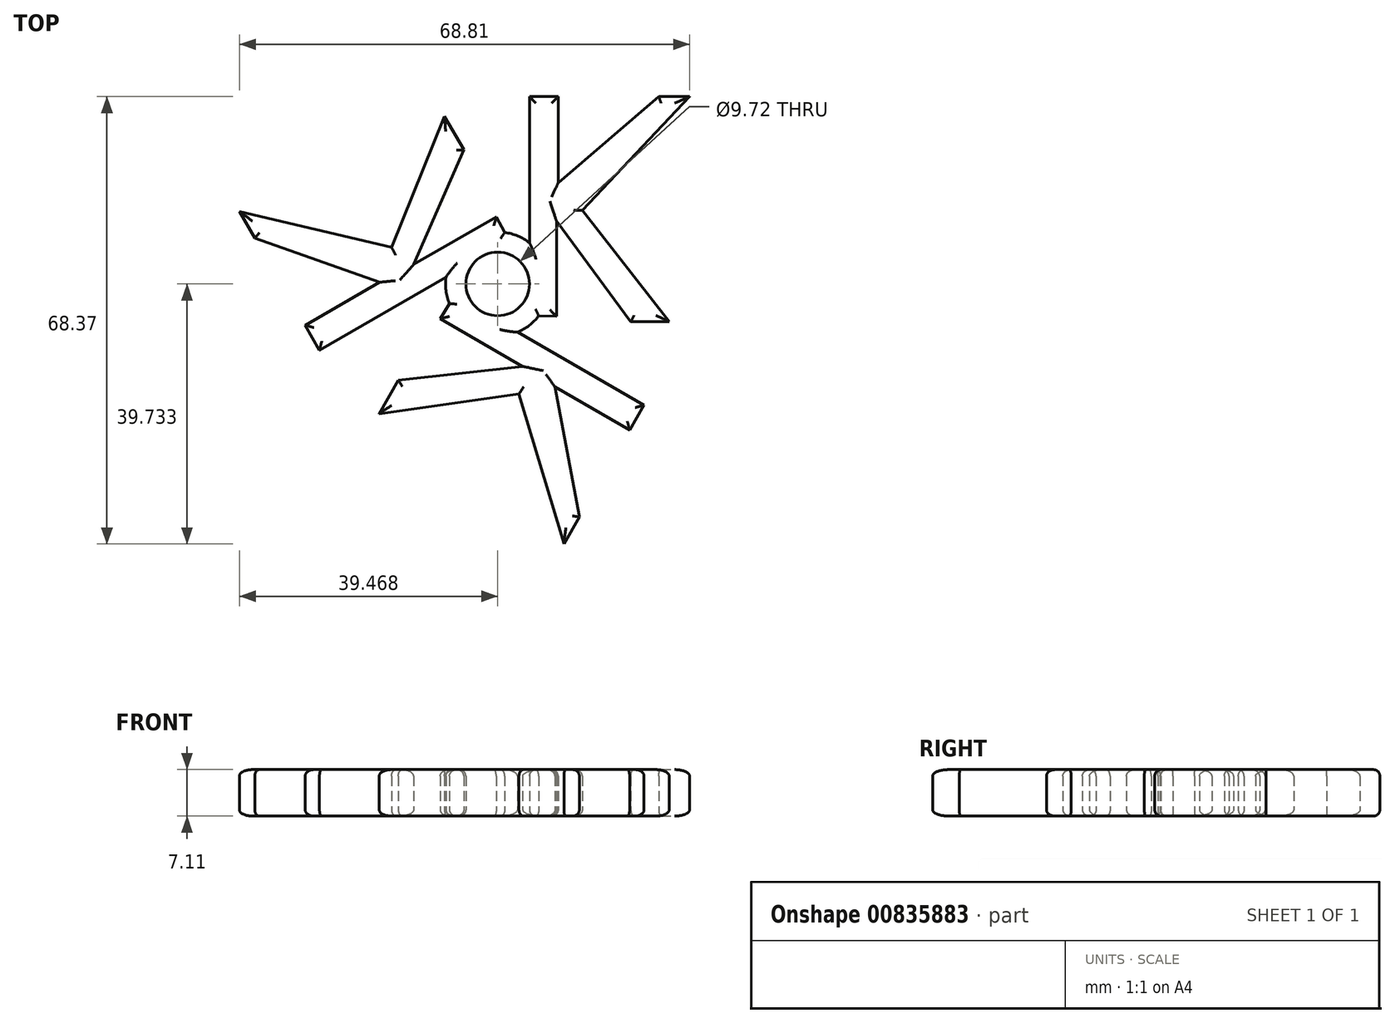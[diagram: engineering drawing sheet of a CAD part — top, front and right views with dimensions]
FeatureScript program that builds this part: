
annotation { "Feature Type Name" : "Feature", "Feature Type Description" : "" }
export const myFeature = defineFeature(function(context is Context, id is Id, definition is map)
    precondition{}
    {
        {
            var Q0;
            Q0=qCreatedBy(makeId("Top.planeOp"),FACE);
            var sketch = newSketch(context, id + "F0", { "sketchPlane" : qUnion([Q0])});
            skText(sketch, "E0", { "text": "K", "fontName": "RobotoSlab-Bold.ttf"});
            skLineSegment(sketch, "E1", {"start": v(-36.74, 28.94) * mm, "end": v(-41.1, 29.85) * mm});
            skLineSegment(sketch, "E2", {"start": v(-41.1, 29.85) * mm, "end": v(-41.1, 34.7) * mm});
            skLineSegment(sketch, "E3", {"start": v(-41.1, 34.7) * mm, "end": v(-24.32, 34.7) * mm});
            skLineSegment(sketch, "E4", {"start": v(-24.32, 34.7) * mm, "end": v(-24.32, 29.8) * mm});
            skLineSegment(sketch, "E5", {"start": v(-24.32, 29.8) * mm, "end": v(-28.43, 28.94) * mm});
            skLineSegment(sketch, "E6", {"start": v(-28.43, 28.94) * mm, "end": v(-28.43, 18) * mm});
            skLineSegment(sketch, "E7", {"start": v(-28.43, 18) * mm, "end": v(-24.89, 18) * mm});
            skLineSegment(sketch, "E8", {"start": v(-24.89, 18) * mm, "end": v(-17.02, 29.37) * mm});
            skLineSegment(sketch, "E9", {"start": v(-17.02, 29.37) * mm, "end": v(-19.35, 29.8) * mm});
            skLineSegment(sketch, "E10", {"start": v(-19.35, 29.8) * mm, "end": v(-19.35, 34.7) * mm});
            skLineSegment(sketch, "E11", {"start": v(-19.35, 34.7) * mm, "end": v(-3, 34.7) * mm});
            skLineSegment(sketch, "E12", {"start": v(-3, 34.7) * mm, "end": v(-3, 29.8) * mm});
            skLineSegment(sketch, "E13", {"start": v(-3, 29.8) * mm, "end": v(-7.33, 29.07) * mm});
            skLineSegment(sketch, "E14", {"start": v(-7.33, 29.07) * mm, "end": v(-17.58, 15.36) * mm});
            skLineSegment(sketch, "E15", {"start": v(-17.58, 15.36) * mm, "end": v(-6.25, -0.86) * mm});
            skLineSegment(sketch, "E16", {"start": v(-6.25, -0.86) * mm, "end": v(-2.14, -1.5) * mm});
            skLineSegment(sketch, "E17", {"start": v(-2.14, -1.5) * mm, "end": v(-2.14, -6.47) * mm});
            skLineSegment(sketch, "E18", {"start": v(-2.14, -6.47) * mm, "end": v(-18.49, -6.47) * mm});
            skLineSegment(sketch, "E19", {"start": v(-18.49, -6.47) * mm, "end": v(-18.49, -1.64) * mm});
            skLineSegment(sketch, "E20", {"start": v(-18.49, -1.64) * mm, "end": v(-16.02, -1.2) * mm});
            skLineSegment(sketch, "E21", {"start": v(-16.02, -1.2) * mm, "end": v(-23.98, 10.73) * mm});
            skLineSegment(sketch, "E22", {"start": v(-23.98, 10.73) * mm, "end": v(-28.43, 10.73) * mm});
            skLineSegment(sketch, "E23", {"start": v(-28.43, 10.73) * mm, "end": v(-28.43, -0.69) * mm});
            skLineSegment(sketch, "E24", {"start": v(-28.43, -0.69) * mm, "end": v(-24.32, -1.64) * mm});
            skLineSegment(sketch, "E25", {"start": v(-24.32, -1.64) * mm, "end": v(-24.32, -6.47) * mm});
            skLineSegment(sketch, "E26", {"start": v(-24.32, -6.47) * mm, "end": v(-41.15, -6.47) * mm});
            skLineSegment(sketch, "E27", {"start": v(-41.15, -6.47) * mm, "end": v(-41.15, -1.6) * mm});
            skLineSegment(sketch, "E28", {"start": v(-41.15, -1.6) * mm, "end": v(-36.7, -0.6) * mm});
            skLineSegment(sketch, "E29", {"start": v(-36.7, -0.6) * mm, "end": v(-36.74, 28.94) * mm});
            skLineSegment(sketch, "E30", {"start": v(18.07, -63.92) * mm, "end": v(18.07, -30.43) * mm});
            skLineSegment(sketch, "E31", {"start": v(18.07, -30.43) * mm, "end": v(22.46, -30.43) * mm});
            skLineSegment(sketch, "E32", {"start": v(22.46, -30.43) * mm, "end": v(22.46, -43.6) * mm});
            skLineSegment(sketch, "E33", {"start": v(22.46, -43.6) * mm, "end": v(37.82, -30.43) * mm});
            skLineSegment(sketch, "E34", {"start": v(37.82, -30.43) * mm, "end": v(42.55, -30.43) * mm});
            skLineSegment(sketch, "E35", {"start": v(42.55, -30.43) * mm, "end": v(26.15, -47.83) * mm});
            skLineSegment(sketch, "E36", {"start": v(26.15, -47.83) * mm, "end": v(39.43, -64.84) * mm});
            skLineSegment(sketch, "E37", {"start": v(39.43, -64.84) * mm, "end": v(33.55, -64.85) * mm});
            skLineSegment(sketch, "E38", {"start": v(33.55, -64.85) * mm, "end": v(22.2, -49.45) * mm});
            skLineSegment(sketch, "E39", {"start": v(22.2, -49.45) * mm, "end": v(22.2, -64.02) * mm});
            skLineSegment(sketch, "E40", {"start": v(22.2, -64.02) * mm, "end": v(18.07, -63.92) * mm});
            skLineSegment(sketch, "E41.1.0", {"start": v(-3, -53.47) * mm, "end": v(5.1, -33.47) * mm});
            skLineSegment(sketch, "E41.1.1", {"start": v(14.98, -52.43) * mm, "end": v(-14.02, -69.17) * mm});
            skLineSegment(sketch, "E41.1.2", {"start": v(5.1, -33.47) * mm, "end": v(8.05, -38.56) * mm});
            skLineSegment(sketch, "E41.1.3", {"start": v(-14.02, -69.17) * mm, "end": v(-16.22, -65.37) * mm});
            skLineSegment(sketch, "E41.1.4", {"start": v(-4.82, -58.8) * mm, "end": v(-23.9, -52.07) * mm});
            skLineSegment(sketch, "E41.1.5", {"start": v(-26.26, -47.97) * mm, "end": v(-3, -53.47) * mm});
            skLineSegment(sketch, "E41.1.6", {"start": v(0.39, -56.09) * mm, "end": v(13, -48.8) * mm});
            skLineSegment(sketch, "E41.1.7", {"start": v(-16.22, -65.37) * mm, "end": v(-4.82, -58.8) * mm});
            skLineSegment(sketch, "E41.1.8", {"start": v(13, -48.8) * mm, "end": v(14.98, -52.43) * mm});
            skLineSegment(sketch, "E41.1.9", {"start": v(-23.9, -52.07) * mm, "end": v(-26.26, -47.97) * mm});
            skLineSegment(sketch, "E41.1.10", {"start": v(8.05, -38.56) * mm, "end": v(0.39, -56.09) * mm});
            skLineSegment(sketch, "E41.2.0", {"start": v(16.47, -75.9) * mm, "end": v(-4.9, -78.9) * mm});
            skLineSegment(sketch, "E41.2.1", {"start": v(6.58, -60.85) * mm, "end": v(35.57, -77.6) * mm});
            skLineSegment(sketch, "E41.2.2", {"start": v(-4.9, -78.9) * mm, "end": v(-1.97, -73.79) * mm});
            skLineSegment(sketch, "E41.2.3", {"start": v(35.57, -77.6) * mm, "end": v(33.38, -81.4) * mm});
            skLineSegment(sketch, "E41.2.4", {"start": v(21.98, -74.82) * mm, "end": v(25.7, -94.7) * mm});
            skLineSegment(sketch, "E41.2.5", {"start": v(23.33, -98.8) * mm, "end": v(16.47, -75.9) * mm});
            skLineSegment(sketch, "E41.2.6", {"start": v(17.04, -71.66) * mm, "end": v(4.42, -64.38) * mm});
            skLineSegment(sketch, "E41.2.7", {"start": v(33.38, -81.4) * mm, "end": v(21.98, -74.82) * mm});
            skLineSegment(sketch, "E41.2.8", {"start": v(4.42, -64.38) * mm, "end": v(6.58, -60.85) * mm});
            skLineSegment(sketch, "E41.2.9", {"start": v(25.7, -94.7) * mm, "end": v(23.33, -98.8) * mm});
            skLineSegment(sketch, "E41.2.10", {"start": v(-1.97, -73.79) * mm, "end": v(17.04, -71.66) * mm});
            skPoint(sketch, "E41.center", {"position": v(13.2, -59.07) * mm});
            skCircle(sketch, "E42", {"center": v(13.2, -59.07) * mm, "radius": 7.96 * mm});
            skCircle(sketch, "E43", {"center": v(13.2, -59.07) * mm, "radius": 4.86 * mm});
            const initialGuessF0  = {"E0": [-0.0427, -0.00647, 1, 0, 0.04175]};
            skSetInitialGuess(sketch, initialGuessF0);
            skSolve(sketch);
        }
        {
            var Q0;
            {var subQ1=sQuery(id+"F0.wireOp",EDGE,"E31");Q0=makeQuery(id+"F0.imprint","IMPRINT",FACE,{"disambiguationData":[TD([[makeQuery(id+"F0.imprint","IMPRINT",EDGE,{"derivedFrom":subQ1}),-1.0]])]});}
            var Q1;
            Q1=makeQuery(id+"F0.imprint","IMPRINT",FACE,{"disambiguationData":[TD([[makeQuery(id+"F0.imprint","IMPRINT",EDGE,{"derivedFrom":sQuery(id+"F0.wireOp",EDGE,"E41.1.0")}),-1.0]])]});
            var Q2;
            Q2=makeQuery(id+"F0.imprint","IMPRINT",FACE,{"disambiguationData":[TD([[makeQuery(id+"F0.imprint","IMPRINT",EDGE,{"derivedFrom":sQuery(id+"F0.wireOp",EDGE,"E41.2.0")}),-1.0]])]});
            var Q3;
            {var subQ0=sQuery(id+"F0.wireOp",EDGE,"E41.2.8");var subQ1=sQuery(id+"F0.wireOp",EDGE,"E41.2.1");var subQ2=makeQuery(id+"F0.imprint","INTERSECT",VERTEX,{"derivedFrom":[subQ1,subQ0]});Q3=makeQuery(id+"F0.imprint","IMPRINT",FACE,{"disambiguationData":[TD([[makeQuery(id+"F0.imprint","IMPRINT",EDGE,{"disambiguationData":[TD([[subQ2,-1.0]])],"derivedFrom":subQ1}),-1.0]])]});}
            var Q4;
            Q4=makeQuery(id+"F0.imprint","IMPRINT",FACE,{"disambiguationData":[TD([[makeQuery(id+"F0.imprint","IMPRINT",EDGE,{"derivedFrom":sQuery(id+"F0.wireOp",EDGE,"E43")}),-1.0]])]});
            var Q5;
            {var subQ0=sQuery(id+"F0.wireOp",EDGE,"E41.1.8");var subQ1=sQuery(id+"F0.wireOp",EDGE,"E41.1.1");var subQ2=makeQuery(id+"F0.imprint","INTERSECT",VERTEX,{"derivedFrom":[subQ1,subQ0]});Q5=makeQuery(id+"F0.imprint","IMPRINT",FACE,{"disambiguationData":[TD([[makeQuery(id+"F0.imprint","IMPRINT",EDGE,{"disambiguationData":[TD([[subQ2,-1.0]])],"derivedFrom":subQ1}),-1.0]])]});}
            var Q6;
            {var subQ0=sQuery(id+"F0.wireOp",EDGE,"E40");var subQ1=sQuery(id+"F0.wireOp",EDGE,"E30");var subQ2=makeQuery(id+"F0.imprint","INTERSECT",VERTEX,{"derivedFrom":[subQ1,subQ0]});Q6=makeQuery(id+"F0.imprint","IMPRINT",FACE,{"disambiguationData":[TD([[makeQuery(id+"F0.imprint","IMPRINT",EDGE,{"disambiguationData":[TD([[subQ2,-1.0]])],"derivedFrom":subQ1}),-1.0]])]});}
            extrude(context, id + "F1", {"entities" : qUnion([Q0, Q1, Q2, Q3, Q4, Q5, Q6]), "depth" : 7.11 * mm, "offsetDistance" : 25.4 * mm});
        }
        {
            var Q0;
            Q0=makeQuery(id+"F1.opExtrude","CAP_FACE",FACE,{"disambiguationData":[OSD([sQuery(id+"F0.wireOp",EDGE,"E30"),sQuery(id+"F0.wireOp",EDGE,"E31"),sQuery(id+"F0.wireOp",EDGE,"E32"),sQuery(id+"F0.wireOp",EDGE,"E33"),sQuery(id+"F0.wireOp",EDGE,"E34"),sQuery(id+"F0.wireOp",EDGE,"E35"),sQuery(id+"F0.wireOp",EDGE,"E36"),sQuery(id+"F0.wireOp",EDGE,"E37"),sQuery(id+"F0.wireOp",EDGE,"E38"),sQuery(id+"F0.wireOp",EDGE,"E39"),sQuery(id+"F0.wireOp",EDGE,"E40"),sQuery(id+"F0.wireOp",EDGE,"E41.1.0"),sQuery(id+"F0.wireOp",EDGE,"E41.1.1"),sQuery(id+"F0.wireOp",EDGE,"E41.1.2"),sQuery(id+"F0.wireOp",EDGE,"E41.1.3"),sQuery(id+"F0.wireOp",EDGE,"E41.1.4"),sQuery(id+"F0.wireOp",EDGE,"E41.1.5"),sQuery(id+"F0.wireOp",EDGE,"E41.1.6"),sQuery(id+"F0.wireOp",EDGE,"E41.1.7"),sQuery(id+"F0.wireOp",EDGE,"E41.1.8"),sQuery(id+"F0.wireOp",EDGE,"E41.1.9"),sQuery(id+"F0.wireOp",EDGE,"E41.1.10"),sQuery(id+"F0.wireOp",EDGE,"E41.2.0"),sQuery(id+"F0.wireOp",EDGE,"E41.2.1"),sQuery(id+"F0.wireOp",EDGE,"E41.2.2"),sQuery(id+"F0.wireOp",EDGE,"E41.2.3"),sQuery(id+"F0.wireOp",EDGE,"E41.2.4"),sQuery(id+"F0.wireOp",EDGE,"E41.2.5"),sQuery(id+"F0.wireOp",EDGE,"E41.2.6"),sQuery(id+"F0.wireOp",EDGE,"E41.2.7"),sQuery(id+"F0.wireOp",EDGE,"E41.2.8"),sQuery(id+"F0.wireOp",EDGE,"E41.2.9"),sQuery(id+"F0.wireOp",EDGE,"E41.2.10"),sQuery(id+"F0.wireOp",EDGE,"E42"),sQuery(id+"F0.wireOp",EDGE,"E43")])],"isStart":false});
            var Q1;
            Q1=makeQuery(id+"F1.opExtrude","CAP_FACE",FACE,{"disambiguationData":[OSD([sQuery(id+"F0.wireOp",EDGE,"E30"),sQuery(id+"F0.wireOp",EDGE,"E31"),sQuery(id+"F0.wireOp",EDGE,"E32"),sQuery(id+"F0.wireOp",EDGE,"E33"),sQuery(id+"F0.wireOp",EDGE,"E34"),sQuery(id+"F0.wireOp",EDGE,"E35"),sQuery(id+"F0.wireOp",EDGE,"E36"),sQuery(id+"F0.wireOp",EDGE,"E37"),sQuery(id+"F0.wireOp",EDGE,"E38"),sQuery(id+"F0.wireOp",EDGE,"E39"),sQuery(id+"F0.wireOp",EDGE,"E40"),sQuery(id+"F0.wireOp",EDGE,"E41.1.0"),sQuery(id+"F0.wireOp",EDGE,"E41.1.1"),sQuery(id+"F0.wireOp",EDGE,"E41.1.2"),sQuery(id+"F0.wireOp",EDGE,"E41.1.3"),sQuery(id+"F0.wireOp",EDGE,"E41.1.4"),sQuery(id+"F0.wireOp",EDGE,"E41.1.5"),sQuery(id+"F0.wireOp",EDGE,"E41.1.6"),sQuery(id+"F0.wireOp",EDGE,"E41.1.7"),sQuery(id+"F0.wireOp",EDGE,"E41.1.8"),sQuery(id+"F0.wireOp",EDGE,"E41.1.9"),sQuery(id+"F0.wireOp",EDGE,"E41.1.10"),sQuery(id+"F0.wireOp",EDGE,"E41.2.0"),sQuery(id+"F0.wireOp",EDGE,"E41.2.1"),sQuery(id+"F0.wireOp",EDGE,"E41.2.2"),sQuery(id+"F0.wireOp",EDGE,"E41.2.3"),sQuery(id+"F0.wireOp",EDGE,"E41.2.4"),sQuery(id+"F0.wireOp",EDGE,"E41.2.5"),sQuery(id+"F0.wireOp",EDGE,"E41.2.6"),sQuery(id+"F0.wireOp",EDGE,"E41.2.7"),sQuery(id+"F0.wireOp",EDGE,"E41.2.8"),sQuery(id+"F0.wireOp",EDGE,"E41.2.9"),sQuery(id+"F0.wireOp",EDGE,"E41.2.10"),sQuery(id+"F0.wireOp",EDGE,"E42"),sQuery(id+"F0.wireOp",EDGE,"E43")])],"isStart":true});
            fillet(context, id + "F2", {"entities" : qUnion([Q0, Q1]), "radius" : 1 * mm, "tangentPropagation" : true, "allowEdgeOverflow" : false});
        }
    });
